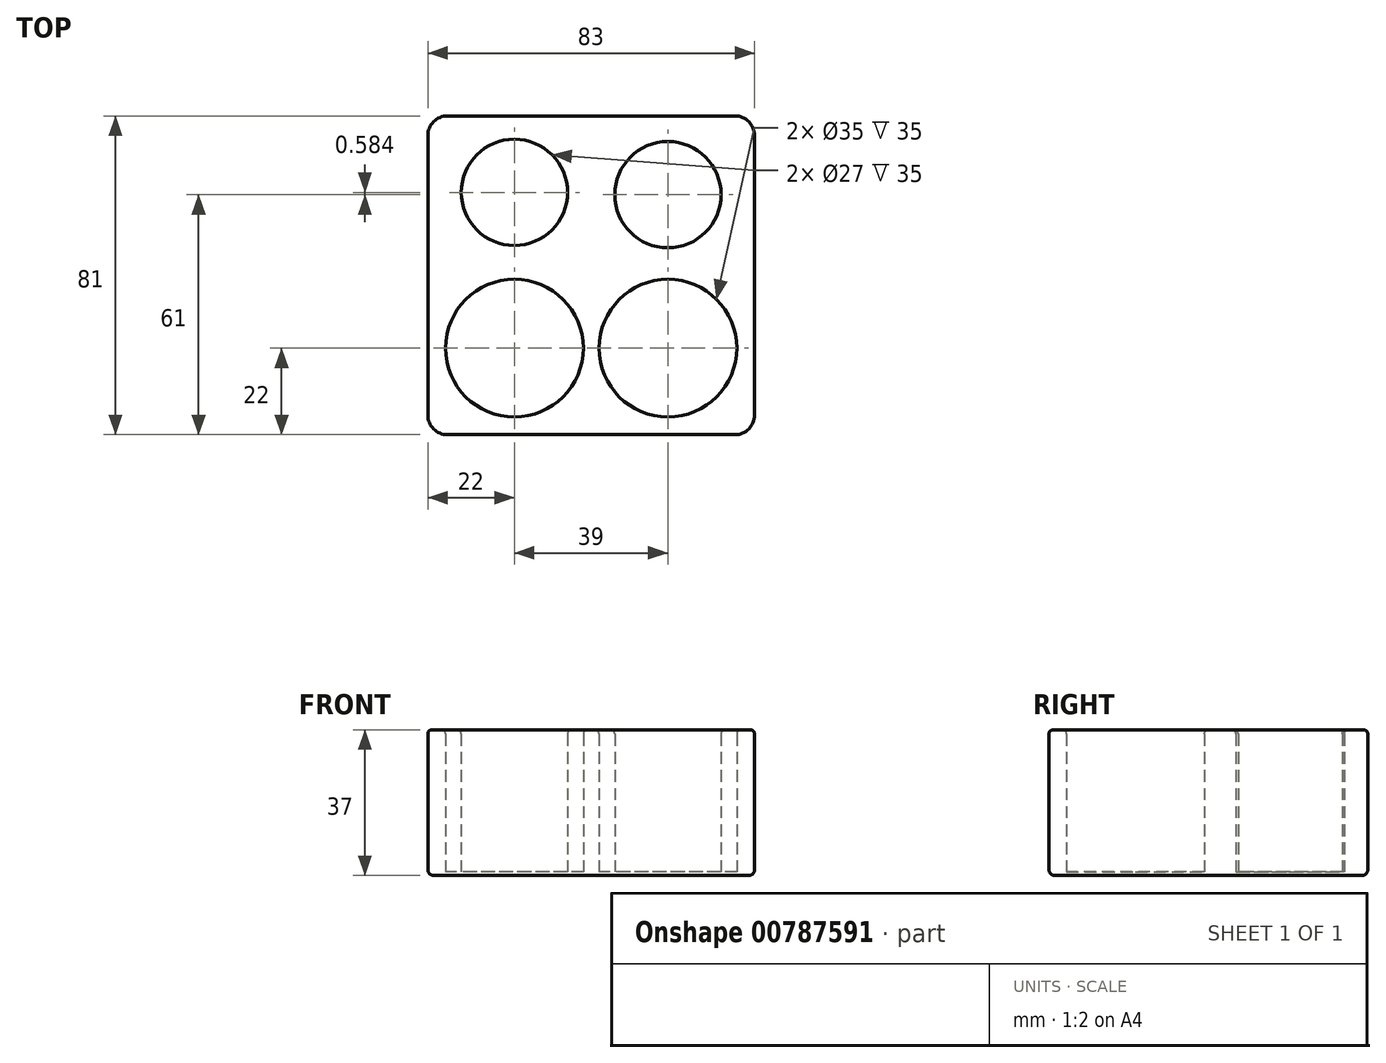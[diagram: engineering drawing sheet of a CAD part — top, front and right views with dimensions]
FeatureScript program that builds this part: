
annotation { "Feature Type Name" : "Feature", "Feature Type Description" : "" }
export const myFeature = defineFeature(function(context is Context, id is Id, definition is map)
    precondition{}
    {
        {
            var Q0;
            Q0=qCreatedBy(makeId("Top.planeOp"),FACE);
            var sketch = newSketch(context, id + "F0", { "sketchPlane" : qUnion([Q0])});
            skPoint(sketch, "E0.middle", {"position": v(0, 0) * mm});
            skCircle(sketch, "E1", {"center": v(-22.5, 0) * mm, "radius": 17.5 * mm});
            skCircle(sketch, "E2", {"center": v(16.5, 0) * mm, "radius": 17.5 * mm});
            skCircle(sketch, "E3", {"center": v(-22.5, 39.58) * mm, "radius": 13.5 * mm});
            skCircle(sketch, "E4", {"center": v(16.5, 39) * mm, "radius": 13.5 * mm});
            skPoint(sketch, "E0.top.end.orphan", {"position": v(47.5, -50) * mm});
            skPoint(sketch, "E0.left.end.orphan", {"position": v(-47.5, -50) * mm});
            skPoint(sketch, "E5.orphan", {"position": v(47.5, 50) * mm});
            skPoint(sketch, "E6.orphan", {"position": v(-47.5, 50) * mm});
            skLineSegment(sketch, "E7.bottom", {"start": v(-44.5, 59) * mm, "end": v(38.5, 59) * mm});
            skLineSegment(sketch, "E7.top", {"start": v(-44.5, -22) * mm, "end": v(38.5, -22) * mm});
            skLineSegment(sketch, "E7.left", {"start": v(-44.5, 59) * mm, "end": v(-44.5, -22) * mm});
            skLineSegment(sketch, "E7.right", {"start": v(38.5, 59) * mm, "end": v(38.5, -22) * mm});
            skSolve(sketch);
        }
        {
            var Q0;
            Q0=qSketchRegion(id+"F0",true);
            var Q1;
            Q1=makeQuery(id+"F0.imprint","IMPRINT",FACE,{"disambiguationData":[TD([[makeQuery(id+"F0.imprint","IMPRINT",EDGE,{"derivedFrom":sQuery(id+"F0.wireOp",EDGE,"E0.bottom")}),-1.0]])]});
            extrude(context, id + "F1", {"entities" : qUnion([Q0, Q1]), "depth" : 36 * mm, "offsetDistance" : 25 * mm});
        }
        {
            var Q0;
            Q0=makeQuery(id+"F1.opExtrude","CAP_FACE",FACE,{"disambiguationData":[OSD([sQuery(id+"F0.wireOp",EDGE,"E1"),sQuery(id+"F0.wireOp",EDGE,"E2"),sQuery(id+"F0.wireOp",EDGE,"E3"),sQuery(id+"F0.wireOp",EDGE,"E4"),sQuery(id+"F0.wireOp",EDGE,"E7.bottom"),sQuery(id+"F0.wireOp",EDGE,"E7.top"),sQuery(id+"F0.wireOp",EDGE,"E7.left"),sQuery(id+"F0.wireOp",EDGE,"E7.right")])],"isStart":false});
            fillet(context, id + "F2", {"entities" : qUnion([Q0]), "radius" : 1 * mm, "tangentPropagation" : true, "allowEdgeOverflow" : false});
        }
        {
            var Q0;
            Q0=makeQuery(id+"F1.opExtrude","CAP_FACE",FACE,{"disambiguationData":[OSD([sQuery(id+"F0.wireOp",EDGE,"E1"),sQuery(id+"F0.wireOp",EDGE,"E2"),sQuery(id+"F0.wireOp",EDGE,"E3"),sQuery(id+"F0.wireOp",EDGE,"E4"),sQuery(id+"F0.wireOp",EDGE,"E7.bottom"),sQuery(id+"F0.wireOp",EDGE,"E7.top"),sQuery(id+"F0.wireOp",EDGE,"E7.left"),sQuery(id+"F0.wireOp",EDGE,"E7.right")])],"isStart":true});
            var sketch = newSketch(context, id + "F3", { "sketchPlane" : qUnion([Q0])});
            skLineSegment(sketch, "E8.bottom", {"start": v(-44.5, 22) * mm, "end": v(38.5, 22) * mm});
            skLineSegment(sketch, "E8.top", {"start": v(-44.5, -59) * mm, "end": v(38.5, -59) * mm});
            skLineSegment(sketch, "E8.left", {"start": v(-44.5, 22) * mm, "end": v(-44.5, -59) * mm});
            skLineSegment(sketch, "E8.right", {"start": v(38.5, 22) * mm, "end": v(38.5, -59) * mm});
            skSolve(sketch);
        }
        {
            var Q0;
            Q0=qSketchRegion(id+"F3",true);
            extrude(context, id + "F4", {"entities" : qUnion([Q0]), "operationType" : NewBodyOperationType.ADD, "depth" : 1 * mm, "offsetDistance" : 25 * mm});
        }
        {
            var Q0;
            Q0=makeQuery(id+"F4.boolean.opBoolean","MERGE",EDGE,{"derivedFrom":[makeQuery(id+"F1.opExtrude","SWEPT_EDGE",EDGE,{"disambiguationData":[OSD([sQuery(id+"F0.wireOp",EDGE,"E7.bottom"),sQuery(id+"F0.wireOp",EDGE,"E7.left")])]}),makeQuery(id+"F4.opExtrude","SWEPT_EDGE",EDGE,{"disambiguationData":[OSD([sQuery(id+"F3.wireOp",EDGE,"E8.top"),sQuery(id+"F3.wireOp",EDGE,"E8.left")])]})]});
            var Q1;
            Q1=makeQuery(id+"F4.boolean.opBoolean","MERGE",EDGE,{"derivedFrom":[makeQuery(id+"F1.opExtrude","SWEPT_EDGE",EDGE,{"disambiguationData":[OSD([sQuery(id+"F0.wireOp",EDGE,"E7.top"),sQuery(id+"F0.wireOp",EDGE,"E7.left")])]}),makeQuery(id+"F4.opExtrude","SWEPT_EDGE",EDGE,{"disambiguationData":[OSD([sQuery(id+"F3.wireOp",EDGE,"E8.bottom"),sQuery(id+"F3.wireOp",EDGE,"E8.left")])]})]});
            var Q2;
            Q2=makeQuery(id+"F4.boolean.opBoolean","MERGE",EDGE,{"derivedFrom":[makeQuery(id+"F1.opExtrude","SWEPT_EDGE",EDGE,{"disambiguationData":[OSD([sQuery(id+"F0.wireOp",EDGE,"E7.top"),sQuery(id+"F0.wireOp",EDGE,"E7.right")])]}),makeQuery(id+"F4.opExtrude","SWEPT_EDGE",EDGE,{"disambiguationData":[OSD([sQuery(id+"F3.wireOp",EDGE,"E8.bottom"),sQuery(id+"F3.wireOp",EDGE,"E8.right")])]})]});
            var Q3;
            Q3=makeQuery(id+"F4.boolean.opBoolean","MERGE",EDGE,{"derivedFrom":[makeQuery(id+"F1.opExtrude","SWEPT_EDGE",EDGE,{"disambiguationData":[OSD([sQuery(id+"F0.wireOp",EDGE,"E7.bottom"),sQuery(id+"F0.wireOp",EDGE,"E7.right")])]}),makeQuery(id+"F4.opExtrude","SWEPT_EDGE",EDGE,{"disambiguationData":[OSD([sQuery(id+"F3.wireOp",EDGE,"E8.top"),sQuery(id+"F3.wireOp",EDGE,"E8.right")])]})]});
            fillet(context, id + "F5", {"entities" : qUnion([Q0, Q1, Q2, Q3]), "radius" : 5 * mm, "tangentPropagation" : true, "allowEdgeOverflow" : false});
        }
        {
            var Q0;
            Q0=makeQuery(id+"F4.opExtrude","CAP_FACE",FACE,{"disambiguationData":[OSD([sQuery(id+"F3.wireOp",EDGE,"E8.bottom"),sQuery(id+"F3.wireOp",EDGE,"E8.top"),sQuery(id+"F3.wireOp",EDGE,"E8.left"),sQuery(id+"F3.wireOp",EDGE,"E8.right")])],"isStart":false});
            fillet(context, id + "F6", {"entities" : qUnion([Q0]), "radius" : 1.5 * mm, "tangentPropagation" : true, "allowEdgeOverflow" : false});
        }
    });
